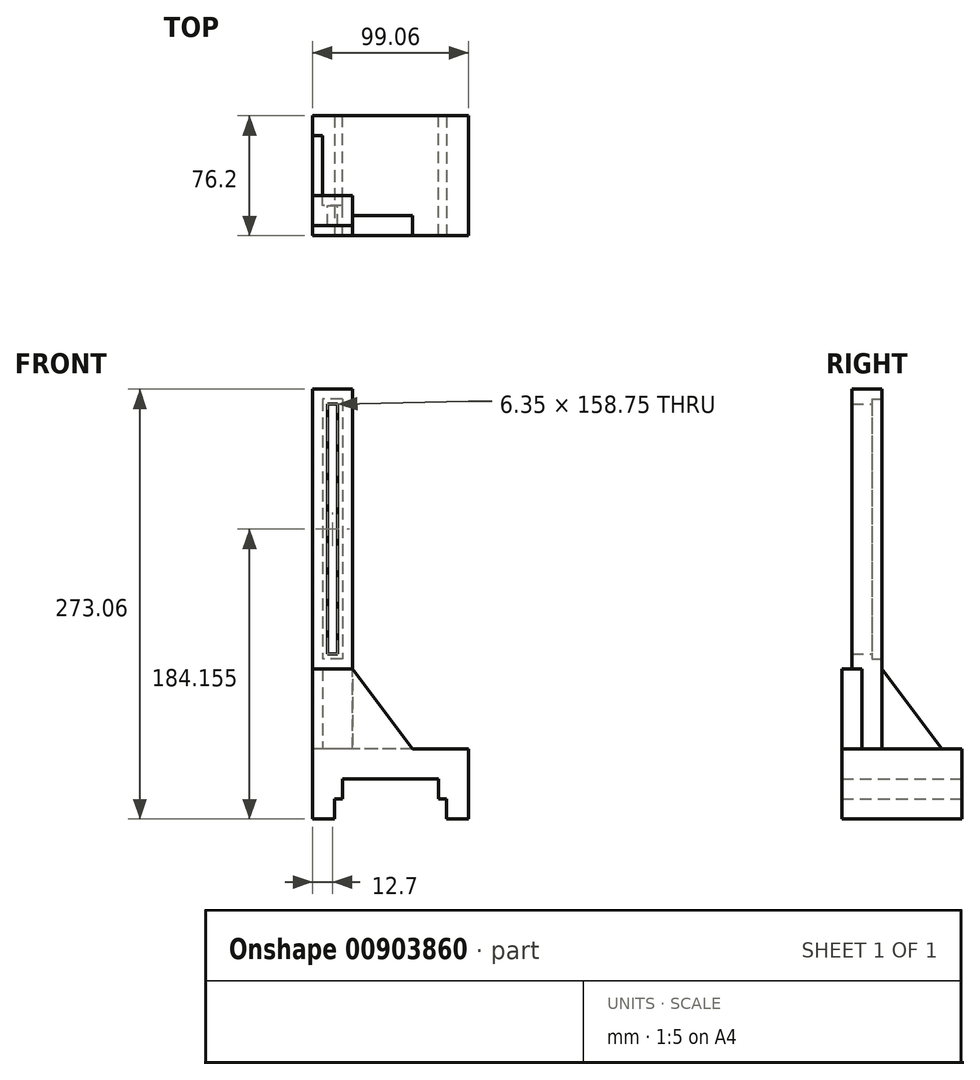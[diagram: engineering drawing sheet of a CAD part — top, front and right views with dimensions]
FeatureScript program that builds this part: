
annotation { "Feature Type Name" : "Feature", "Feature Type Description" : "" }
export const myFeature = defineFeature(function(context is Context, id is Id, definition is map)
    precondition{}
    {
        {
            var Q0;
            Q0=qCreatedBy(makeId("Front.planeOp"),FACE);
            var sketch = newSketch(context, id + "F0", { "sketchPlane" : qUnion([Q0])});
            skLineSegment(sketch, "E0.bottom", {"start": v(49.53, -22.23) * mm, "end": v(-49.53, -22.23) * mm});
            skLineSegment(sketch, "E0.top", {"start": v(49.53, 22.23) * mm, "end": v(-49.53, 22.23) * mm});
            skLineSegment(sketch, "E0.left", {"start": v(49.53, -22.23) * mm, "end": v(49.53, 22.23) * mm});
            skLineSegment(sketch, "E0.right", {"start": v(-49.53, -22.23) * mm, "end": v(-49.53, 22.22) * mm});
            skPoint(sketch, "E0.middle", {"position": v(0, 0) * mm});
            skLineSegment(sketch, "E1.bottom", {"start": v(30.48, -47.63) * mm, "end": v(-30.48, -47.63) * mm});
            skLineSegment(sketch, "E1.top", {"start": v(30.48, 3.18) * mm, "end": v(-30.48, 3.18) * mm});
            skLineSegment(sketch, "E1.left", {"start": v(30.48, -47.63) * mm, "end": v(30.48, 3.18) * mm});
            skLineSegment(sketch, "E1.right", {"start": v(-30.48, -47.63) * mm, "end": v(-30.48, 3.18) * mm});
            skPoint(sketch, "E1.middle", {"position": v(0, -22.23) * mm});
            skSolve(sketch);
        }
        {
            var Q0;
            Q0=makeQuery(id+"F0.imprint","IMPRINT",FACE,{"disambiguationData":[TD([[makeQuery(id+"F0.imprint","IMPRINT",EDGE,{"derivedFrom":sQuery(id+"F0.wireOp",EDGE,"E0.top")}),1.0]])]});
            extrude(context, id + "F1", {"entities" : qUnion([Q0]), "endBound" : BoundingType.SYMMETRIC, "depth" : 76.2 * mm, "offsetDistance" : 25.4 * mm});
        }
        {
            var Q0;
            Q0=qCreatedBy(makeId("Front.planeOp"),FACE);
            var sketch = newSketch(context, id + "F2", { "sketchPlane" : qUnion([Q0])});
            skLineSegment(sketch, "E2.bottom", {"start": v(35.56, -36.92) * mm, "end": v(-35.56, -36.92) * mm});
            skLineSegment(sketch, "E2.top", {"start": v(35.56, -9.52) * mm, "end": v(-35.56, -9.53) * mm});
            skLineSegment(sketch, "E2.left", {"start": v(35.56, -36.92) * mm, "end": v(35.56, -9.53) * mm});
            skLineSegment(sketch, "E2.right", {"start": v(-35.56, -36.92) * mm, "end": v(-35.56, -9.53) * mm});
            skPoint(sketch, "E2.middle", {"position": v(0, -23.22) * mm});
            skSolve(sketch);
        }
        {
            var Q0;
            Q0=makeQuery(id+"F2.imprint","IMPRINT",FACE,{"disambiguationData":[TD([[makeQuery(id+"F2.imprint","IMPRINT",EDGE,{"derivedFrom":sQuery(id+"F2.wireOp",EDGE,"E2.bottom")}),-1.0]])]});
            extrude(context, id + "F3", {"entities" : qUnion([Q0]), "operationType" : NewBodyOperationType.REMOVE, "endBound" : BoundingType.SYMMETRIC, "oppositeDirection" : true, "depth" : 101.6 * mm, "offsetDistance" : 25.4 * mm});
        }
        {
            var Q0;
            Q0=makeQuery(id+"F1.opExtrude","SWEPT_FACE",FACE,{"disambiguationData":[OSD([sQuery(id+"F0.wireOp",EDGE,"E0.top")])]});
            var sketch = newSketch(context, id + "F4", { "sketchPlane" : qUnion([Q0])});
            skPoint(sketch, "E3.right.end.orphan", {"position": v(-7.9, -5.96) * mm});
            skPoint(sketch, "E3.bottom.end.orphan", {"position": v(-7.9, -51.19) * mm});
            skLineSegment(sketch, "E4.bottom", {"start": v(-24.13, -31.75) * mm, "end": v(-49.53, -31.75) * mm});
            skLineSegment(sketch, "E4.top", {"start": v(-24.13, -12.7) * mm, "end": v(-49.53, -12.7) * mm});
            skLineSegment(sketch, "E4.left", {"start": v(-24.13, -31.75) * mm, "end": v(-24.13, -12.7) * mm});
            skLineSegment(sketch, "E4.right", {"start": v(-49.53, -31.75) * mm, "end": v(-49.53, -12.7) * mm});
            skPoint(sketch, "E4.middle", {"position": v(-36.83, -22.23) * mm});
            skSolve(sketch);
        }
        {
            var Q0;
            Q0=qSketchRegion(id+"F4",true);
            extrude(context, id + "F5", {"entities" : qUnion([Q0]), "operationType" : NewBodyOperationType.ADD, "depth" : 228.6 * mm, "offsetDistance" : 25.4 * mm});
        }
        {
            var Q0;
            Q0=makeQuery(id+"F1.opExtrude","CAP_FACE",FACE,{"disambiguationData":[OSD([sQuery(id+"F0.wireOp",EDGE,"E0.bottom"),sQuery(id+"F0.wireOp",EDGE,"E0.top"),sQuery(id+"F0.wireOp",EDGE,"E0.left"),sQuery(id+"F0.wireOp",EDGE,"E0.right"),sQuery(id+"F0.wireOp",EDGE,"E1.top"),sQuery(id+"F0.wireOp",EDGE,"E1.left"),sQuery(id+"F0.wireOp",EDGE,"E1.right")])],"isStart":false});
            var sketch = newSketch(context, id + "F6", { "sketchPlane" : qUnion([Q0])});
            skLineSegment(sketch, "E5.bottom", {"start": v(-49.53, 22.22) * mm, "end": v(-24.13, 22.22) * mm});
            skLineSegment(sketch, "E5.top", {"start": v(-49.53, 73.03) * mm, "end": v(-24.13, 73.03) * mm});
            skLineSegment(sketch, "E5.left", {"start": v(-49.53, 22.22) * mm, "end": v(-49.53, 73.03) * mm});
            skLineSegment(sketch, "E5.right", {"start": v(-24.13, 22.22) * mm, "end": v(-24.13, 73.03) * mm});
            skLineSegment(sketch, "E6", {"start": v(-24.13, 22.22) * mm, "end": v(13.97, 22.23) * mm});
            skLineSegment(sketch, "E7", {"start": v(-24.13, 73.03) * mm, "end": v(13.97, 22.23) * mm});
            skSolve(sketch);
        }
        {
            var Q0;
            Q0=qSketchRegion(id+"F6",true);
            extrude(context, id + "F7", {"entities" : qUnion([Q0]), "operationType" : NewBodyOperationType.ADD, "oppositeDirection" : true, "depth" : 12.7 * mm, "offsetDistance" : 25.4 * mm});
        }
        {
            var Q0;
            Q0=makeQuery(id+"F7.boolean.opBoolean","MERGE",FACE,{"derivedFrom":[makeQuery(id+"F5.boolean.opBoolean","MERGE",FACE,{"derivedFrom":[makeQuery(id+"F1.opExtrude","SWEPT_FACE",FACE,{"disambiguationData":[OSD([sQuery(id+"F0.wireOp",EDGE,"E0.right")])]}),makeQuery(id+"F5.opExtrude","SWEPT_FACE",FACE,{"disambiguationData":[OSD([sQuery(id+"F4.wireOp",EDGE,"E4.right")])]})]}),makeQuery(id+"F7.opExtrude","SWEPT_FACE",FACE,{"disambiguationData":[OSD([sQuery(id+"F6.wireOp",EDGE,"E5.left")])]})]});
            var sketch = newSketch(context, id + "F8", { "sketchPlane" : qUnion([Q0])});
            skLineSegment(sketch, "E8", {"start": v(12.7, 22.23) * mm, "end": v(-25.4, 22.23) * mm});
            skLineSegment(sketch, "E9", {"start": v(12.7, 22.23) * mm, "end": v(12.7, 73.03) * mm});
            skLineSegment(sketch, "E10", {"start": v(-25.4, 22.22) * mm, "end": v(12.7, 73.03) * mm});
            skSolve(sketch);
        }
        {
            var Q0;
            Q0=qSketchRegion(id+"F8",true);
            extrude(context, id + "F9", {"entities" : qUnion([Q0]), "operationType" : NewBodyOperationType.ADD, "oppositeDirection" : true, "depth" : 6.35 * mm, "offsetDistance" : 25.4 * mm});
        }
        {
            var Q0;
            Q0=makeQuery(id+"F5.opExtrude","SWEPT_FACE",FACE,{"disambiguationData":[OSD([sQuery(id+"F4.wireOp",EDGE,"E4.top")])]});
            var sketch = newSketch(context, id + "F10", { "sketchPlane" : qUnion([Q0])});
            skLineSegment(sketch, "E11.bottom", {"start": v(30.48, 244.48) * mm, "end": v(43.18, 244.48) * mm});
            skLineSegment(sketch, "E11.top", {"start": v(30.48, 79.38) * mm, "end": v(43.18, 79.38) * mm});
            skLineSegment(sketch, "E11.left", {"start": v(30.48, 244.48) * mm, "end": v(30.48, 79.38) * mm});
            skLineSegment(sketch, "E11.right", {"start": v(43.18, 244.48) * mm, "end": v(43.18, 79.38) * mm});
            skPoint(sketch, "E11.middle", {"position": v(36.83, 161.93) * mm});
            skSolve(sketch);
        }
        {
            var Q0;
            Q0=makeQuery(id+"F10.imprint","IMPRINT",FACE,{"disambiguationData":[TD([[makeQuery(id+"F10.imprint","IMPRINT",EDGE,{"derivedFrom":sQuery(id+"F10.wireOp",EDGE,"E11.bottom")}),-1.0]])]});
            extrude(context, id + "F11", {"entities" : qUnion([Q0]), "operationType" : NewBodyOperationType.REMOVE, "oppositeDirection" : true, "depth" : 6.35 * mm, "offsetDistance" : 25.4 * mm});
        }
        {
            var Q0;
            Q0=makeQuery(id+"F11.boolean.opBoolean","COPY",FACE,{"derivedFrom":makeQuery(id+"F11.opExtrude","CAP_FACE",FACE,{"disambiguationData":[OSD([sQuery(id+"F10.wireOp",EDGE,"E11.bottom"),sQuery(id+"F10.wireOp",EDGE,"E11.top"),sQuery(id+"F10.wireOp",EDGE,"E11.left"),sQuery(id+"F10.wireOp",EDGE,"E11.right")])],"isStart":false})});
            var sketch = newSketch(context, id + "F12", { "sketchPlane" : qUnion([Q0])});
            skLineSegment(sketch, "E12.bottom", {"start": v(40, 241.3) * mm, "end": v(33.66, 241.3) * mm});
            skLineSegment(sketch, "E12.top", {"start": v(40, 82.55) * mm, "end": v(33.66, 82.55) * mm});
            skLineSegment(sketch, "E12.left", {"start": v(40, 241.3) * mm, "end": v(40, 82.55) * mm});
            skLineSegment(sketch, "E12.right", {"start": v(33.66, 241.3) * mm, "end": v(33.66, 82.55) * mm});
            skSolve(sketch);
        }
        {
            var Q0;
            Q0=makeQuery(id+"F12.imprint","IMPRINT",FACE,{"disambiguationData":[TD([[makeQuery(id+"F12.imprint","IMPRINT",EDGE,{"derivedFrom":sQuery(id+"F12.wireOp",EDGE,"E12.bottom")}),1.0]])]});
            extrude(context, id + "F13", {"entities" : qUnion([Q0]), "operationType" : NewBodyOperationType.REMOVE, "oppositeDirection" : true, "depth" : 25.4 * mm, "offsetDistance" : 25.4 * mm});
        }
        {
            var Q0;
            Q0=makeQuery(id+"F5.opExtrude","SWEPT_FACE",FACE,{"disambiguationData":[OSD([sQuery(id+"F4.wireOp",EDGE,"E4.top")])]});
            var sketch = newSketch(context, id + "F14", { "sketchPlane" : qUnion([Q0])});
            skLineSegment(sketch, "E13.bottom", {"start": v(43.18, 263.53) * mm, "end": v(30.48, 263.53) * mm});
            skLineSegment(sketch, "E13.top", {"start": v(43.18, 238.13) * mm, "end": v(30.48, 238.13) * mm});
            skLineSegment(sketch, "E13.left", {"start": v(43.18, 263.53) * mm, "end": v(43.18, 238.13) * mm});
            skLineSegment(sketch, "E13.right", {"start": v(30.48, 263.53) * mm, "end": v(30.48, 238.13) * mm});
            skPoint(sketch, "E13.middle", {"position": v(36.83, 250.83) * mm});
            skSolve(sketch);
        }
        {
            var Q0;
            {var subQ0=sQuery(id+"F14.wireOp",EDGE,"E13.bottom");Q0=makeQuery(id+"F14.imprint","IMPRINT",FACE,{"disambiguationData":[TD([[makeQuery(id+"F14.imprint","IMPRINT",EDGE,{"derivedFrom":subQ0}),1.0]])]});}
            var Q1;
            {var subQ0=sQuery(id+"F14.wireOp",EDGE,"E13.top");Q1=makeQuery(id+"F14.imprint","IMPRINT",FACE,{"disambiguationData":[TD([[makeQuery(id+"F14.imprint","IMPRINT",EDGE,{"derivedFrom":subQ0}),-1.0]])]});}
            var Q2;
            {var subQ1=makeQuery(id+"F11.boolean.opBoolean","COPY",EDGE,{"derivedFrom":makeQuery(id+"F11.opExtrude","CAP_EDGE",EDGE,{"disambiguationData":[OSD([sQuery(id+"F10.wireOp",EDGE,"E11.bottom")])],"isStart":true})});Q2=makeQuery(id+"F14.imprint","IMPRINT",FACE,{"disambiguationData":[TD([[makeQuery(id+"F14.imprint","IMPRINT",EDGE,{"derivedFrom":subQ1}),1.0]])]});}
            extrude(context, id + "F15", {"entities" : qUnion([Q0, Q1, Q2]), "operationType" : NewBodyOperationType.REMOVE, "oppositeDirection" : true, "depth" : 6.35 * mm, "offsetDistance" : 25.4 * mm});
        }
    });
